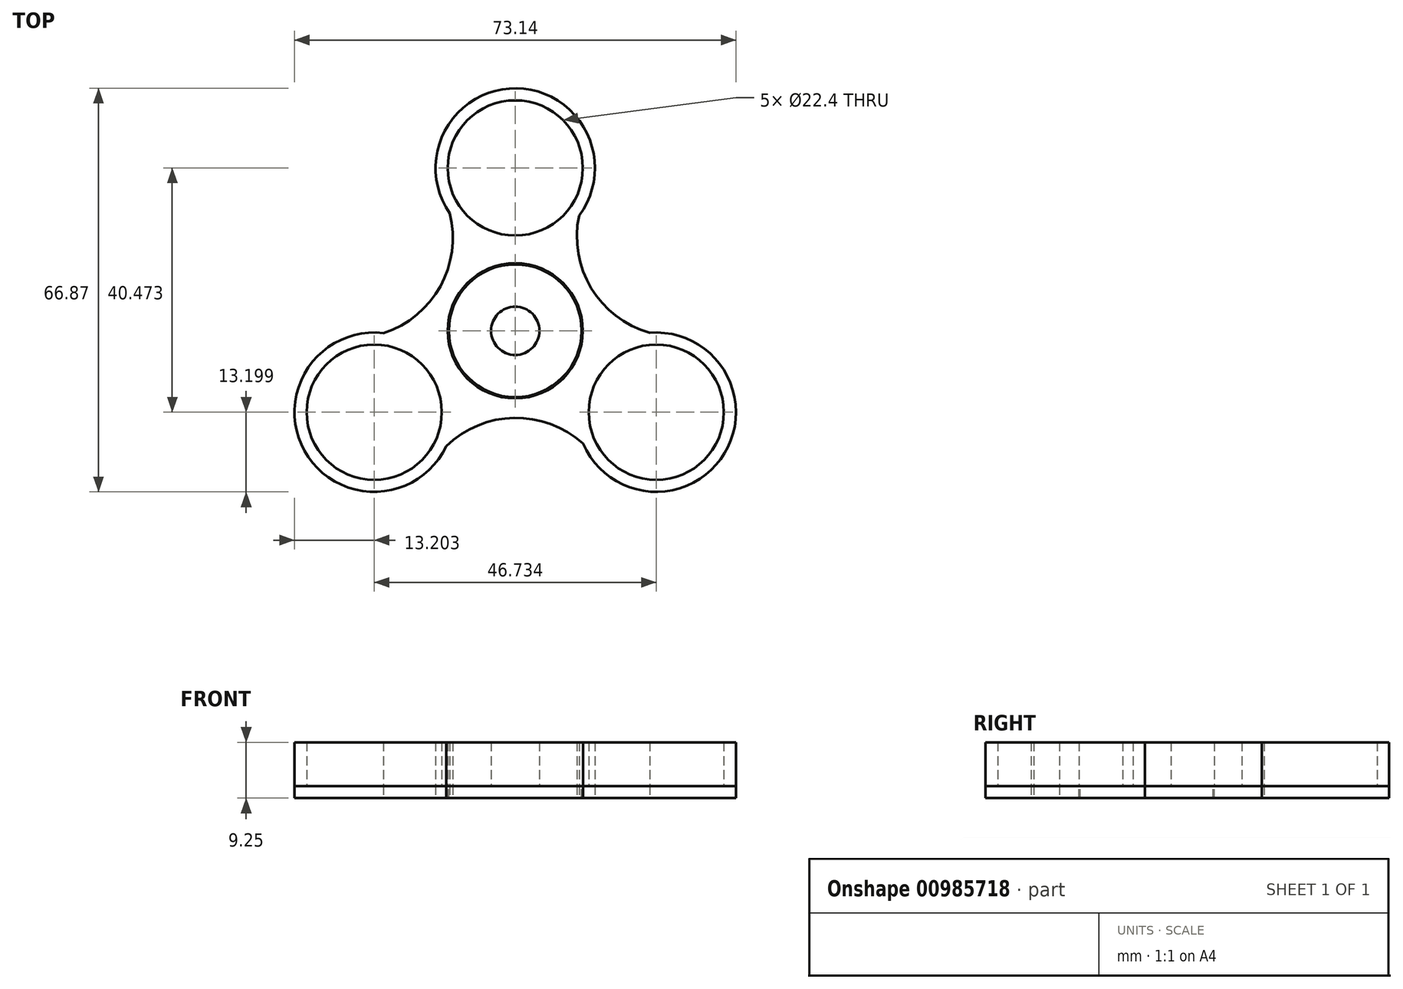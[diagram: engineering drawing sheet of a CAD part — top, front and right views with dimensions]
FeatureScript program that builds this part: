
annotation { "Feature Type Name" : "Feature", "Feature Type Description" : "" }
export const myFeature = defineFeature(function(context is Context, id is Id, definition is map)
    precondition{}
    {
        {
            var Q0;
            Q0=qCreatedBy(makeId("Top.planeOp"),FACE);
            var sketch = newSketch(context, id + "F0", { "sketchPlane" : qUnion([Q0])});
            skArc(sketch, "E0", {"start": v(10.58, 19.08) * mm, "mid": v(0.23, 40.18) * mm, "end": v(-10.84, 19.45) * mm});
            skArc(sketch, "E1.1.0", {"start": v(-21.81, -0.38) * mm, "mid": v(-34.91, -19.9) * mm, "end": v(-11.43, -19.12) * mm});
            skArc(sketch, "E1.2.0", {"start": v(11.24, -18.7) * mm, "mid": v(34.68, -20.29) * mm, "end": v(22.27, -0.34) * mm});
            skPoint(sketch, "E1.center", {"position": v(0, 0) * mm});
            skArc(sketch, "E2", {"start": v(-21.81, -0.38) * mm, "mid": v(-12.41, 7.37) * mm, "end": v(-10.84, 19.45) * mm});
            skArc(sketch, "E3.1.0", {"start": v(11.24, -18.7) * mm, "mid": v(-0.18, -14.44) * mm, "end": v(-11.43, -19.12) * mm});
            skArc(sketch, "E3.2.0", {"start": v(10.58, 19.08) * mm, "mid": v(12.6, 7.07) * mm, "end": v(22.27, -0.34) * mm});
            skSolve(sketch);
        }
        {
            var Q0;
            Q0=makeQuery(id+"F0.imprint","IMPRINT",FACE,{"disambiguationData":[TD([[makeQuery(id+"F0.imprint","IMPRINT",EDGE,{"derivedFrom":sQuery(id+"F0.wireOp",EDGE,"E0")}),1.0]])]});
            extrude(context, id + "F1", {"entities" : qUnion([Q0]), "depth" : 2 * mm, "offsetDistance" : 25 * mm});
        }
        {
            var Q0;
            Q0=makeQuery(id+"F1.opExtrude","CAP_FACE",FACE,{"disambiguationData":[OSD([sQuery(id+"F0.wireOp",EDGE,"E0"),sQuery(id+"F0.wireOp",EDGE,"E1.1.0"),sQuery(id+"F0.wireOp",EDGE,"E1.2.0"),sQuery(id+"F0.wireOp",EDGE,"E2"),sQuery(id+"F0.wireOp",EDGE,"E3.1.0"),sQuery(id+"F0.wireOp",EDGE,"E3.2.0")])],"isStart":false});
            var sketch = newSketch(context, id + "F2", { "sketchPlane" : qUnion([Q0])});
            skCircle(sketch, "E4", {"center": v(0, 0) * mm, "radius": 11.2 * mm});
            skCircle(sketch, "E5", {"center": v(0, 26.98) * mm, "radius": 11.2 * mm});
            skCircle(sketch, "E6.1.0", {"center": v(-23.37, -13.5) * mm, "radius": 11.2 * mm});
            skCircle(sketch, "E6.2.0", {"center": v(23.37, -13.5) * mm, "radius": 11.2 * mm});
            skCircle(sketch, "E7", {"center": v(0, 0) * mm, "radius": 4 * mm});
            skSolve(sketch);
        }
        {
            var Q0;
            Q0=makeQuery(id+"F2.imprint","IMPRINT",FACE,{"disambiguationData":[TD([[makeQuery(id+"F2.imprint","IMPRINT",EDGE,{"derivedFrom":sQuery(id+"F2.wireOp",EDGE,"E4")}),-1.0]])]});
            var sketch = newSketch(context, id + "F3", { "sketchPlane" : qUnion([Q0])});
            skCircle(sketch, "E8", {"center": v(0, 0) * mm, "radius": 11.2 * mm});
            skCircle(sketch, "E9", {"center": v(0, 0) * mm, "radius": 11 * mm});
            skSolve(sketch);
        }
        {
            var Q0;
            Q0 = qSketchRegion(id + "F3", true);
            var Q1;
            Q1=makeQuery(id+"F1.opExtrude","CAP_FACE",FACE,{"disambiguationData":[OSD([sQuery(id+"F0.wireOp",EDGE,"E0"),sQuery(id+"F0.wireOp",EDGE,"E1.1.0"),sQuery(id+"F0.wireOp",EDGE,"E1.2.0"),sQuery(id+"F0.wireOp",EDGE,"E2"),sQuery(id+"F0.wireOp",EDGE,"E3.1.0"),sQuery(id+"F0.wireOp",EDGE,"E3.2.0")])],"isStart":true});
            extrude(context, id + "F4", {"entities" : qUnion([Q0, Q1]), "operationType" : NewBodyOperationType.REMOVE, "oppositeDirection" : true, "depth" : 2 * mm, "offsetDistance" : 25 * mm});
        }
        {
            var Q0;
            Q0=makeQuery(id+"F2.imprint","IMPRINT",FACE,{"disambiguationData":[TD([[makeQuery(id+"F2.imprint","IMPRINT",EDGE,{"derivedFrom":sQuery(id+"F2.wireOp",EDGE,"E4")}),-1.0]])]});
            var Q1;
            Q1=makeQuery(id+"F2.imprint","IMPRINT",FACE,{"disambiguationData":[TD([[makeQuery(id+"F2.imprint","IMPRINT",EDGE,{"derivedFrom":sQuery(id+"F2.wireOp",EDGE,"E7")}),1.0]])]});
            extrude(context, id + "F5", {"entities" : qUnion([Q0, Q1]), "depth" : 7.25 * mm, "offsetDistance" : 25 * mm});
        }
        {
            var Q0;
            Q0=qCreatedBy(makeId("Top.planeOp"),FACE);
            cPlane(context, id + "F6", {"entities" : qUnion([Q0]), "cplaneType" : CPlaneType.OFFSET, "offset" : 9 * mm, "width" : 150 * mm, "height" : 150 * mm});
        }
    });
